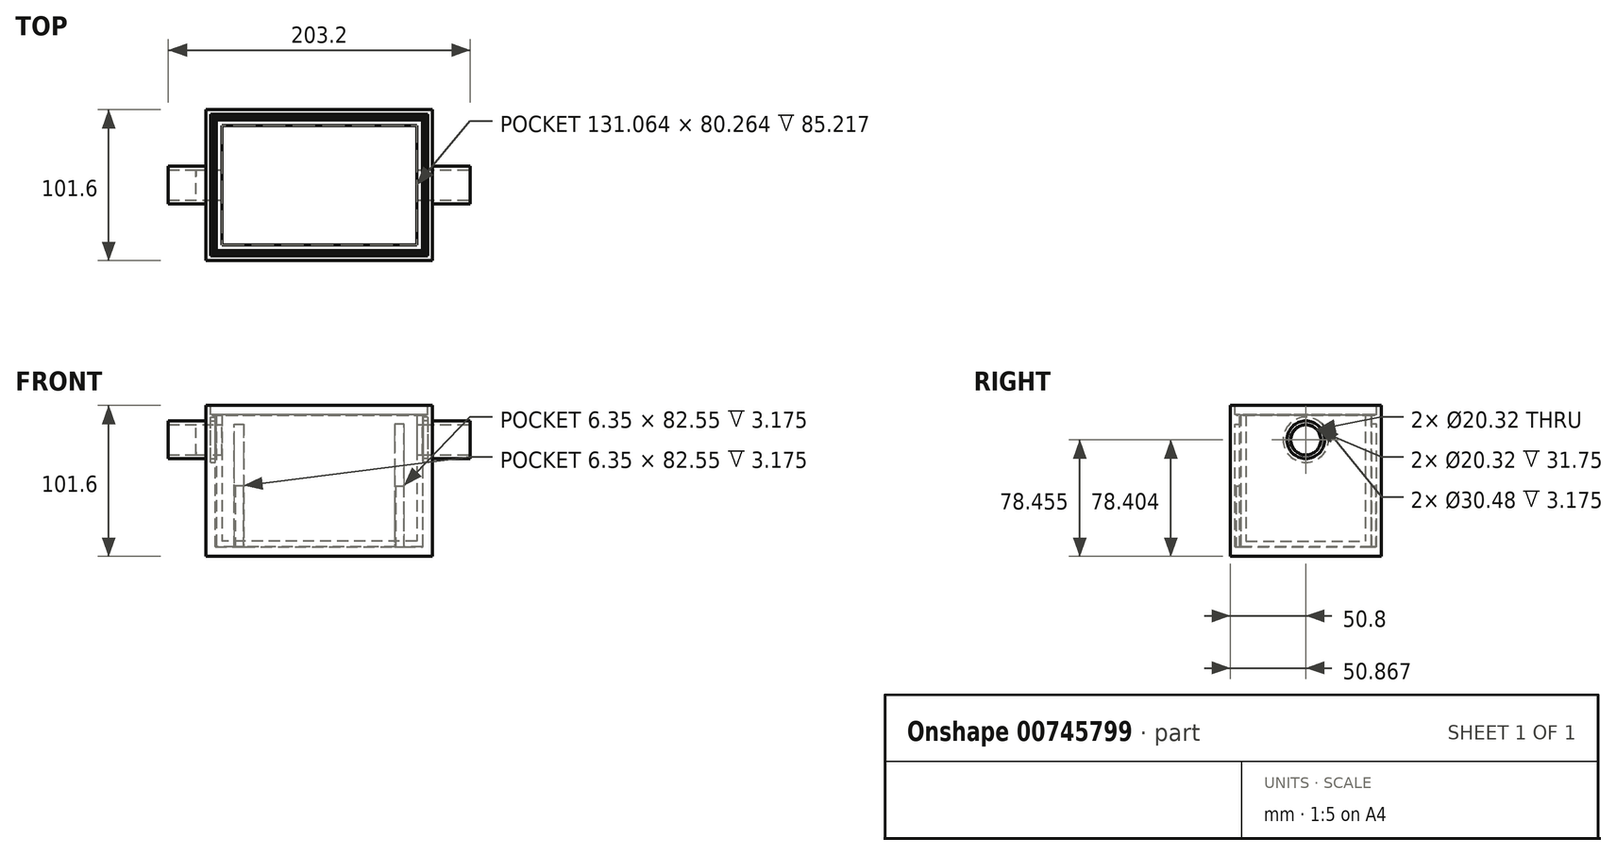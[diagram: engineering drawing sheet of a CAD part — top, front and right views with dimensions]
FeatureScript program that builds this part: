
annotation { "Feature Type Name" : "Feature", "Feature Type Description" : "" }
export const myFeature = defineFeature(function(context is Context, id is Id, definition is map)
    precondition{}
    {
        {
            var Q0;
            Q0=qCreatedBy(makeId("Front.planeOp"),FACE);
            var sketch = newSketch(context, id + "F0", { "sketchPlane" : qUnion([Q0])});
            skLineSegment(sketch, "E0.bottom", {"start": v(-76.2, 50.8) * mm, "end": v(76.2, 50.8) * mm});
            skLineSegment(sketch, "E0.top", {"start": v(-76.2, -50.8) * mm, "end": v(76.2, -50.8) * mm});
            skLineSegment(sketch, "E0.left", {"start": v(-76.2, 50.8) * mm, "end": v(-76.2, -50.8) * mm});
            skLineSegment(sketch, "E0.right", {"start": v(76.2, 50.8) * mm, "end": v(76.2, -50.8) * mm});
            skPoint(sketch, "E0.middle", {"position": v(0, 0) * mm});
            skSolve(sketch);
        }
        {
            var Q0;
            Q0 = qSketchRegion(id + "F0", true);
            extrude(context, id + "F1", {"entities" : qUnion([Q0]), "depth" : 101.6 * mm, "offsetDistance" : 25.4 * mm});
        }
        {
            var Q0;
            Q0=makeQuery(id+"F1.opExtrude","SWEPT_FACE",FACE,{"disambiguationData":[OSD([sQuery(id+"F0.wireOp",EDGE,"E0.left")])]});
            var sketch = newSketch(context, id + "F2", { "sketchPlane" : qUnion([Q0])});
            skCircle(sketch, "E1", {"center": v(50.8, 27.65) * mm, "radius": 12.7 * mm});
            skPoint(sketch, "E1.centerSnap0", {"position": v(50.8, 50.8) * mm});
            skCircle(sketch, "E2", {"center": v(50.8, 27.65) * mm, "radius": 10.16 * mm});
            skSolve(sketch);
        }
        {
            var Q0;
            Q0 = qSketchRegion(id + "F2", true);
            extrude(context, id + "F3", {"entities" : qUnion([Q0]), "operationType" : NewBodyOperationType.ADD, "depth" : 25.4 * mm, "offsetDistance" : 25.4 * mm, "hasSecondDirection" : true, "secondDirectionOppositeDirection" : true, "secondDirectionDepth" : 177.8 * mm});
        }
        {
            var Q0;
            Q0=makeQuery(id+"F3.boolean.opBoolean","SPLIT",FACE,{"disambiguationData":[TD([makeQuery(id+"F3.opExtrude","SWEPT_FACE",FACE,{"disambiguationData":[OSD([sQuery(id+"F2.wireOp",EDGE,"E2")])]})])],"derivedFrom":makeQuery(id+"F1.opExtrude","SWEPT_FACE",FACE,{"disambiguationData":[OSD([sQuery(id+"F0.wireOp",EDGE,"E0.left")])]})});
            var sketch = newSketch(context, id + "F4", { "sketchPlane" : qUnion([Q0])});
            skCircle(sketch, "E3", {"center": v(50.8, 27.65) * mm, "radius": 10.16 * mm});
            skPoint(sketch, "E3.first.point", {"position": v(44.09, 35.28) * mm});
            skPoint(sketch, "E3.second.point", {"position": v(54.89, 36.96) * mm});
            skPoint(sketch, "E3.third.point", {"position": v(59.33, 33.17) * mm});
            skSolve(sketch);
        }
        {
            var Q0;
            Q0 = qSketchRegion(id + "F4", true);
            extrude(context, id + "F5", {"entities" : qUnion([Q0]), "operationType" : NewBodyOperationType.REMOVE, "oppositeDirection" : true, "depth" : 152.4 * mm, "offsetDistance" : 25.4 * mm});
        }
        {
            var Q0;
            Q0=makeQuery(id+"F1.opExtrude","SWEPT_FACE",FACE,{"disambiguationData":[OSD([sQuery(id+"F0.wireOp",EDGE,"E0.bottom")])]});
            var sketch = newSketch(context, id + "F6", { "sketchPlane" : qUnion([Q0])});
            skLineSegment(sketch, "E4.bottom", {"start": v(-69.85, -6.35) * mm, "end": v(69.85, -6.35) * mm});
            skLineSegment(sketch, "E4.top", {"start": v(-69.85, -95.25) * mm, "end": v(69.85, -95.25) * mm});
            skLineSegment(sketch, "E4.left", {"start": v(-69.85, -6.35) * mm, "end": v(-69.85, -95.25) * mm});
            skLineSegment(sketch, "E4.right", {"start": v(69.85, -6.35) * mm, "end": v(69.85, -95.25) * mm});
            skPoint(sketch, "E4.middle", {"position": v(0, -50.8) * mm});
            skPoint(sketch, "E4.middle.positionSnap0", {"position": v(-76.2, -50.8) * mm});
            skPoint(sketch, "E4.middle.positionSnap1", {"position": v(0, 0) * mm});
            skPoint(sketch, "E4.centerSnap0", {"position": v(-76.2, -50.8) * mm});
            skPoint(sketch, "E4.centerSnap1", {"position": v(0, 0) * mm});
            skSolve(sketch);
        }
        {
            var Q0;
            Q0 = qSketchRegion(id + "F6", true);
            extrude(context, id + "F7", {"entities" : qUnion([Q0]), "operationType" : NewBodyOperationType.REMOVE, "oppositeDirection" : true, "depth" : 95.25 * mm, "offsetDistance" : 25.4 * mm});
        }
        {
            var Q0;
            Q0=makeQuery(id+"F1.opExtrude","SWEPT_FACE",FACE,{"disambiguationData":[OSD([sQuery(id+"F0.wireOp",EDGE,"E0.bottom")])]});
            var sketch = newSketch(context, id + "F8", { "sketchPlane" : qUnion([Q0])});
            skLineSegment(sketch, "E5.bottom", {"start": v(73.03, -3.18) * mm, "end": v(-73.03, -3.18) * mm});
            skLineSegment(sketch, "E5.top", {"start": v(73.03, -98.43) * mm, "end": v(-73.03, -98.43) * mm});
            skLineSegment(sketch, "E5.left", {"start": v(73.03, -3.18) * mm, "end": v(73.03, -98.43) * mm});
            skLineSegment(sketch, "E5.right", {"start": v(-73.03, -3.18) * mm, "end": v(-73.03, -98.43) * mm});
            skPoint(sketch, "E5.middle", {"position": v(0, -50.8) * mm});
            skPoint(sketch, "E5.middle.positionSnap0", {"position": v(-69.85, -50.8) * mm});
            skPoint(sketch, "E5.centerSnap0", {"position": v(-69.85, -50.8) * mm});
            skSolve(sketch);
        }
        {
            var Q0;
            Q0 = qSketchRegion(id + "F8", true);
            extrude(context, id + "F9", {"entities" : qUnion([Q0]), "operationType" : NewBodyOperationType.REMOVE, "oppositeDirection" : true, "depth" : 6.35 * mm, "offsetDistance" : 25.4 * mm});
        }
        {
            var Q0;
            Q0=makeQuery(id+"F7.boolean.opBoolean","COPY",FACE,{"derivedFrom":makeQuery(id+"F7.opExtrude","SWEPT_FACE",FACE,{"disambiguationData":[OSD([sQuery(id+"F6.wireOp",EDGE,"E4.bottom")])]})});
            var sketch = newSketch(context, id + "F10", { "sketchPlane" : qUnion([Q0])});
            skLineSegment(sketch, "E6", {"start": v(-57.15, -44.45) * mm, "end": v(-57.15, 38.1) * mm});
            skLineSegment(sketch, "E7", {"start": v(-57.15, 38.1) * mm, "end": v(-50.8, 38.1) * mm});
            skLineSegment(sketch, "E8", {"start": v(-50.8, 38.1) * mm, "end": v(-50.8, -44.45) * mm});
            skLineSegment(sketch, "E9", {"start": v(-50.8, -44.45) * mm, "end": v(-57.15, -44.45) * mm});
            skLineSegment(sketch, "E10", {"start": v(57.15, -44.45) * mm, "end": v(57.15, 38.1) * mm});
            skLineSegment(sketch, "E11", {"start": v(57.15, 38.1) * mm, "end": v(50.8, 38.1) * mm});
            skLineSegment(sketch, "E12", {"start": v(50.8, 38.1) * mm, "end": v(50.8, -44.45) * mm});
            skLineSegment(sketch, "E13", {"start": v(50.8, -44.45) * mm, "end": v(57.15, -44.45) * mm});
            skSolve(sketch);
        }
        {
            var Q0;
            Q0 = qSketchRegion(id + "F10", true);
            extrude(context, id + "F11", {"entities" : qUnion([Q0]), "operationType" : NewBodyOperationType.REMOVE, "oppositeDirection" : true, "depth" : 3.17 * mm, "offsetDistance" : 25.4 * mm});
        }
        {
            var Q0;
            Q0=makeQuery(id+"F9.boolean.opBoolean","COPY",FACE,{"derivedFrom":makeQuery(id+"F9.opExtrude","CAP_FACE",FACE,{"disambiguationData":[OSD([sQuery(id+"F8.wireOp",EDGE,"E5.bottom"),sQuery(id+"F8.wireOp",EDGE,"E5.top"),sQuery(id+"F8.wireOp",EDGE,"E5.left"),sQuery(id+"F8.wireOp",EDGE,"E5.right")])],"isStart":false})});
            var sketch = newSketch(context, id + "F12", { "sketchPlane" : qUnion([Q0])});
            skLineSegment(sketch, "E14.bottom", {"start": v(71.75, -4.45) * mm, "end": v(-71.76, -4.45) * mm});
            skLineSegment(sketch, "E14.top", {"start": v(71.75, -97.16) * mm, "end": v(-71.76, -97.16) * mm});
            skLineSegment(sketch, "E14.left", {"start": v(71.75, -4.45) * mm, "end": v(71.75, -97.16) * mm});
            skLineSegment(sketch, "E14.right", {"start": v(-71.76, -4.45) * mm, "end": v(-71.76, -97.16) * mm});
            skPoint(sketch, "E14.middle", {"position": v(0, -50.8) * mm});
            skPoint(sketch, "E14.middle.positionSnap0", {"position": v(-69.85, -50.8) * mm});
            skPoint(sketch, "E14.middle.positionSnap1", {"position": v(0, -95.25) * mm});
            skPoint(sketch, "E14.centerSnap0", {"position": v(-69.85, -50.8) * mm});
            skPoint(sketch, "E14.centerSnap1", {"position": v(0, -95.25) * mm});
            skLineSegment(sketch, "E15.bottom", {"start": v(71.12, -5.08) * mm, "end": v(-71.12, -5.08) * mm});
            skLineSegment(sketch, "E15.top", {"start": v(71.12, -96.52) * mm, "end": v(-71.12, -96.52) * mm});
            skLineSegment(sketch, "E15.left", {"start": v(71.12, -5.08) * mm, "end": v(71.12, -96.52) * mm});
            skLineSegment(sketch, "E15.right", {"start": v(-71.12, -5.08) * mm, "end": v(-71.12, -96.52) * mm});
            skSolve(sketch);
        }
        {
            var Q0;
            Q0 = qSketchRegion(id + "F12", true);
            extrude(context, id + "F13", {"entities" : qUnion([Q0]), "operationType" : NewBodyOperationType.REMOVE, "oppositeDirection" : true, "depth" : 0.64 * mm, "offsetDistance" : 25.4 * mm});
        }
        {
            var Q0;
            Q0=makeQuery(id+"F7.boolean.opBoolean","COPY",FACE,{"derivedFrom":makeQuery(id+"F7.opExtrude","SWEPT_FACE",FACE,{"disambiguationData":[OSD([sQuery(id+"F6.wireOp",EDGE,"E4.left")])]})});
            var sketch = newSketch(context, id + "F14", { "sketchPlane" : qUnion([Q0])});
            skPoint(sketch, "E16", {"position": v(-41.68, 36.5) * mm});
            skPoint(sketch, "E17", {"position": v(-63.23, 30.24) * mm});
            skPoint(sketch, "E18", {"position": v(-45.27, 16.22) * mm});
            skCircle(sketch, "E19", {"center": v(-50.8, 27.65) * mm, "radius": 12.7 * mm});
            skPoint(sketch, "E20", {"position": v(-39.81, 38.22) * mm});
            skPoint(sketch, "E21", {"position": v(-43.83, 14.1) * mm});
            skPoint(sketch, "E22", {"position": v(-65.64, 31.11) * mm});
            skCircle(sketch, "E23", {"center": v(-50.8, 27.65) * mm, "radius": 15.24 * mm});
            skSolve(sketch);
        }
        {
            var Q0;
            Q0 = qSketchRegion(id + "F14", true);
            extrude(context, id + "F15", {"entities" : qUnion([Q0]), "operationType" : NewBodyOperationType.REMOVE, "oppositeDirection" : true, "depth" : 3.17 * mm, "offsetDistance" : 25.4 * mm});
        }
        {
            var Q0;
            Q0=makeQuery(id+"F7.boolean.opBoolean","COPY",FACE,{"derivedFrom":makeQuery(id+"F7.opExtrude","SWEPT_FACE",FACE,{"disambiguationData":[OSD([sQuery(id+"F6.wireOp",EDGE,"E4.right")])]})});
            var sketch = newSketch(context, id + "F16", { "sketchPlane" : qUnion([Q0])});
            skPoint(sketch, "E24", {"position": v(38.15, 28.8) * mm});
            skPoint(sketch, "E25", {"position": v(35.6, 28.66) * mm});
            skPoint(sketch, "E26", {"position": v(54.32, 15.45) * mm});
            skPoint(sketch, "E27", {"position": v(54.56, 12.88) * mm});
            skPoint(sketch, "E28", {"position": v(58.17, 38) * mm});
            skPoint(sketch, "E29", {"position": v(59.43, 40.22) * mm});
            skCircle(sketch, "E30", {"center": v(50.8, 27.65) * mm, "radius": 12.7 * mm});
            skCircle(sketch, "E31", {"center": v(50.8, 27.65) * mm, "radius": 15.24 * mm});
            skSolve(sketch);
        }
        {
            var Q0;
            Q0 = qSketchRegion(id + "F16", true);
            extrude(context, id + "F17", {"entities" : qUnion([Q0]), "operationType" : NewBodyOperationType.REMOVE, "oppositeDirection" : true, "depth" : 3.17 * mm, "offsetDistance" : 25.4 * mm});
        }
        {
            var Q0;
            Q0=makeQuery(id+"F7.boolean.opBoolean","COPY",FACE,{"derivedFrom":makeQuery(id+"F7.opExtrude","SWEPT_FACE",FACE,{"disambiguationData":[OSD([sQuery(id+"F6.wireOp",EDGE,"E4.top")])]})});
            var sketch = newSketch(context, id + "F18", { "sketchPlane" : qUnion([Q0])});
            skLineSegment(sketch, "E32", {"start": v(57.15, -44.45) * mm, "end": v(57.15, 38.1) * mm});
            skLineSegment(sketch, "E33", {"start": v(57.15, 38.1) * mm, "end": v(50.8, 38.1) * mm});
            skLineSegment(sketch, "E34", {"start": v(50.8, 38.1) * mm, "end": v(50.8, -44.45) * mm});
            skLineSegment(sketch, "E35", {"start": v(-57.15, -44.45) * mm, "end": v(-57.15, 38.1) * mm});
            skLineSegment(sketch, "E36", {"start": v(-57.15, 38.1) * mm, "end": v(-50.8, 38.1) * mm});
            skLineSegment(sketch, "E37", {"start": v(-50.8, 38.1) * mm, "end": v(-50.8, -44.45) * mm});
            skLineSegment(sketch, "E38", {"start": v(57.15, -44.45) * mm, "end": v(50.8, -44.45) * mm});
            skLineSegment(sketch, "E39", {"start": v(-57.15, -44.45) * mm, "end": v(-50.8, -44.45) * mm});
            skSolve(sketch);
        }
        {
            var Q0;
            Q0 = qSketchRegion(id + "F18", true);
            extrude(context, id + "F19", {"entities" : qUnion([Q0]), "operationType" : NewBodyOperationType.REMOVE, "oppositeDirection" : true, "depth" : 3.17 * mm, "offsetDistance" : 25.4 * mm});
        }
        {
            var Q0;
            Q0=makeQuery(id+"F19.boolean.opBoolean","MERGE",FACE,{"derivedFrom":[makeQuery(id+"F11.boolean.opBoolean","MERGE",FACE,{"derivedFrom":[makeQuery(id+"F7.boolean.opBoolean","COPY",FACE,{"derivedFrom":makeQuery(id+"F7.opExtrude","CAP_FACE",FACE,{"disambiguationData":[OSD([sQuery(id+"F6.wireOp",EDGE,"E4.bottom"),sQuery(id+"F6.wireOp",EDGE,"E4.top"),sQuery(id+"F6.wireOp",EDGE,"E4.left"),sQuery(id+"F6.wireOp",EDGE,"E4.right")])],"isStart":false})}),makeQuery(id+"F11.opExtrude","SWEPT_FACE",FACE,{"disambiguationData":[OSD([sQuery(id+"F10.wireOp",EDGE,"E9")])]}),makeQuery(id+"F11.opExtrude","SWEPT_FACE",FACE,{"disambiguationData":[OSD([sQuery(id+"F10.wireOp",EDGE,"E13")])]})]}),makeQuery(id+"F19.opExtrude","SWEPT_FACE",FACE,{"disambiguationData":[OSD([sQuery(id+"F18.wireOp",EDGE,"E38")])]}),makeQuery(id+"F19.opExtrude","SWEPT_FACE",FACE,{"disambiguationData":[OSD([sQuery(id+"F18.wireOp",EDGE,"E39")])]})]});
            var sketch = newSketch(context, id + "F20", { "sketchPlane" : qUnion([Q0])});
            skLineSegment(sketch, "E40", {"start": v(56.64, -97.92) * mm, "end": v(56.64, -94.74) * mm});
            skLineSegment(sketch, "E41", {"start": v(56.64, -94.74) * mm, "end": v(69.34, -94.74) * mm});
            skLineSegment(sketch, "E42", {"start": v(69.34, -94.74) * mm, "end": v(69.34, -6.86) * mm});
            skLineSegment(sketch, "E43", {"start": v(69.34, -6.86) * mm, "end": v(56.64, -6.86) * mm});
            skLineSegment(sketch, "E44", {"start": v(56.64, -6.86) * mm, "end": v(56.64, -3.68) * mm});
            skLineSegment(sketch, "E45", {"start": v(56.64, -3.68) * mm, "end": v(51.3, -3.68) * mm});
            skLineSegment(sketch, "E46", {"start": v(51.3, -3.68) * mm, "end": v(51.3, -6.86) * mm});
            skLineSegment(sketch, "E47", {"start": v(51.3, -6.86) * mm, "end": v(-51.3, -6.86) * mm});
            skLineSegment(sketch, "E48", {"start": v(-51.3, -6.86) * mm, "end": v(-51.3, -3.68) * mm});
            skLineSegment(sketch, "E49", {"start": v(-51.3, -3.68) * mm, "end": v(-56.64, -3.68) * mm});
            skLineSegment(sketch, "E50", {"start": v(-56.64, -3.68) * mm, "end": v(-56.64, -6.86) * mm});
            skLineSegment(sketch, "E51", {"start": v(-56.64, -6.86) * mm, "end": v(-69.34, -6.86) * mm});
            skLineSegment(sketch, "E52", {"start": v(-69.34, -6.86) * mm, "end": v(-69.34, -94.74) * mm});
            skLineSegment(sketch, "E53", {"start": v(-69.34, -94.74) * mm, "end": v(-56.64, -94.74) * mm});
            skLineSegment(sketch, "E54", {"start": v(-56.64, -94.74) * mm, "end": v(-56.64, -97.92) * mm});
            skLineSegment(sketch, "E55", {"start": v(-56.64, -97.92) * mm, "end": v(-51.3, -97.92) * mm});
            skLineSegment(sketch, "E56", {"start": v(-51.3, -97.92) * mm, "end": v(-51.3, -94.74) * mm});
            skLineSegment(sketch, "E57", {"start": v(-51.3, -94.74) * mm, "end": v(51.3, -94.74) * mm});
            skLineSegment(sketch, "E58", {"start": v(51.3, -94.74) * mm, "end": v(51.3, -97.92) * mm});
            skLineSegment(sketch, "E59", {"start": v(51.3, -97.92) * mm, "end": v(56.64, -97.92) * mm});
            skSolve(sketch);
        }
        {
            var Q0;
            Q0 = qSketchRegion(id + "F20", true);
            extrude(context, id + "F21", {"entities" : qUnion([Q0]), "depth" : 82.04 * mm, "offsetDistance" : 25.4 * mm});
        }
        {
            var Q0;
            Q0=makeQuery(id+"F21.opExtrude","CAP_FACE",FACE,{"disambiguationData":[OSD([sQuery(id+"F20.wireOp",EDGE,"E40"),sQuery(id+"F20.wireOp",EDGE,"E41"),sQuery(id+"F20.wireOp",EDGE,"E42"),sQuery(id+"F20.wireOp",EDGE,"E43"),sQuery(id+"F20.wireOp",EDGE,"E44"),sQuery(id+"F20.wireOp",EDGE,"E45"),sQuery(id+"F20.wireOp",EDGE,"E46"),sQuery(id+"F20.wireOp",EDGE,"E47"),sQuery(id+"F20.wireOp",EDGE,"E48"),sQuery(id+"F20.wireOp",EDGE,"E49"),sQuery(id+"F20.wireOp",EDGE,"E50"),sQuery(id+"F20.wireOp",EDGE,"E51"),sQuery(id+"F20.wireOp",EDGE,"E52"),sQuery(id+"F20.wireOp",EDGE,"E53"),sQuery(id+"F20.wireOp",EDGE,"E54"),sQuery(id+"F20.wireOp",EDGE,"E55"),sQuery(id+"F20.wireOp",EDGE,"E56"),sQuery(id+"F20.wireOp",EDGE,"E57"),sQuery(id+"F20.wireOp",EDGE,"E58"),sQuery(id+"F20.wireOp",EDGE,"E59")])],"isStart":false});
            var sketch = newSketch(context, id + "F22", { "sketchPlane" : qUnion([Q0])});
            skLineSegment(sketch, "E60.bottom", {"start": v(51.3, -6.86) * mm, "end": v(56.64, -6.86) * mm});
            skLineSegment(sketch, "E60.top", {"start": v(51.3, -3.68) * mm, "end": v(56.64, -3.68) * mm});
            skLineSegment(sketch, "E60.left", {"start": v(51.3, -6.86) * mm, "end": v(51.3, -3.68) * mm});
            skLineSegment(sketch, "E60.right", {"start": v(56.64, -6.86) * mm, "end": v(56.64, -3.68) * mm});
            skLineSegment(sketch, "E61.bottom", {"start": v(56.64, -94.74) * mm, "end": v(51.3, -94.74) * mm});
            skLineSegment(sketch, "E61.top", {"start": v(56.64, -97.92) * mm, "end": v(51.3, -97.92) * mm});
            skLineSegment(sketch, "E61.left", {"start": v(56.64, -94.74) * mm, "end": v(56.64, -97.92) * mm});
            skLineSegment(sketch, "E61.right", {"start": v(51.3, -94.74) * mm, "end": v(51.3, -97.92) * mm});
            skLineSegment(sketch, "E62.bottom", {"start": v(-51.3, -94.74) * mm, "end": v(-56.64, -94.74) * mm});
            skLineSegment(sketch, "E62.top", {"start": v(-51.3, -97.92) * mm, "end": v(-56.64, -97.92) * mm});
            skLineSegment(sketch, "E62.left", {"start": v(-51.3, -94.74) * mm, "end": v(-51.3, -97.92) * mm});
            skLineSegment(sketch, "E62.right", {"start": v(-56.64, -94.74) * mm, "end": v(-56.64, -97.92) * mm});
            skLineSegment(sketch, "E63.bottom", {"start": v(-56.64, -6.86) * mm, "end": v(-51.3, -6.86) * mm});
            skLineSegment(sketch, "E63.top", {"start": v(-56.64, -3.68) * mm, "end": v(-51.3, -3.68) * mm});
            skLineSegment(sketch, "E63.left", {"start": v(-56.64, -6.86) * mm, "end": v(-56.64, -3.68) * mm});
            skLineSegment(sketch, "E63.right", {"start": v(-51.3, -6.86) * mm, "end": v(-51.3, -3.68) * mm});
            skSolve(sketch);
        }
        {
            var Q0;
            Q0 = qSketchRegion(id + "F22", true);
            extrude(context, id + "F23", {"entities" : qUnion([Q0]), "operationType" : NewBodyOperationType.REMOVE, "oppositeDirection" : true, "depth" : 41.02 * mm, "offsetDistance" : 25.4 * mm});
        }
        {
            var Q0;
            Q0=makeQuery(id+"F21.opExtrude","CAP_FACE",FACE,{"disambiguationData":[OSD([sQuery(id+"F20.wireOp",EDGE,"E40"),sQuery(id+"F20.wireOp",EDGE,"E41"),sQuery(id+"F20.wireOp",EDGE,"E42"),sQuery(id+"F20.wireOp",EDGE,"E43"),sQuery(id+"F20.wireOp",EDGE,"E44"),sQuery(id+"F20.wireOp",EDGE,"E45"),sQuery(id+"F20.wireOp",EDGE,"E46"),sQuery(id+"F20.wireOp",EDGE,"E47"),sQuery(id+"F20.wireOp",EDGE,"E48"),sQuery(id+"F20.wireOp",EDGE,"E49"),sQuery(id+"F20.wireOp",EDGE,"E50"),sQuery(id+"F20.wireOp",EDGE,"E51"),sQuery(id+"F20.wireOp",EDGE,"E52"),sQuery(id+"F20.wireOp",EDGE,"E53"),sQuery(id+"F20.wireOp",EDGE,"E54"),sQuery(id+"F20.wireOp",EDGE,"E55"),sQuery(id+"F20.wireOp",EDGE,"E56"),sQuery(id+"F20.wireOp",EDGE,"E57"),sQuery(id+"F20.wireOp",EDGE,"E58"),sQuery(id+"F20.wireOp",EDGE,"E59")])],"isStart":false});
            shell(context, id + "F24", {"entities" : qUnion([Q0]), "thickness" : 3.8 * mm});
        }
        {
            var Q0;
            Q0=makeQuery(id+"F21.opExtrude","CAP_FACE",FACE,{"disambiguationData":[OSD([sQuery(id+"F20.wireOp",EDGE,"E40"),sQuery(id+"F20.wireOp",EDGE,"E41"),sQuery(id+"F20.wireOp",EDGE,"E42"),sQuery(id+"F20.wireOp",EDGE,"E43"),sQuery(id+"F20.wireOp",EDGE,"E44"),sQuery(id+"F20.wireOp",EDGE,"E45"),sQuery(id+"F20.wireOp",EDGE,"E46"),sQuery(id+"F20.wireOp",EDGE,"E47"),sQuery(id+"F20.wireOp",EDGE,"E48"),sQuery(id+"F20.wireOp",EDGE,"E49"),sQuery(id+"F20.wireOp",EDGE,"E50"),sQuery(id+"F20.wireOp",EDGE,"E51"),sQuery(id+"F20.wireOp",EDGE,"E52"),sQuery(id+"F20.wireOp",EDGE,"E53"),sQuery(id+"F20.wireOp",EDGE,"E54"),sQuery(id+"F20.wireOp",EDGE,"E55"),sQuery(id+"F20.wireOp",EDGE,"E56"),sQuery(id+"F20.wireOp",EDGE,"E57"),sQuery(id+"F20.wireOp",EDGE,"E58"),sQuery(id+"F20.wireOp",EDGE,"E59")])],"isStart":false});
            var sketch = newSketch(context, id + "F25", { "sketchPlane" : qUnion([Q0])});
            skLineSegment(sketch, "E64.bottom", {"start": v(-65.53, -10.67) * mm, "end": v(65.53, -10.67) * mm});
            skLineSegment(sketch, "E64.top", {"start": v(-65.53, -90.93) * mm, "end": v(65.53, -90.93) * mm});
            skLineSegment(sketch, "E64.left", {"start": v(-65.53, -10.67) * mm, "end": v(-65.53, -90.93) * mm});
            skLineSegment(sketch, "E64.right", {"start": v(65.53, -10.67) * mm, "end": v(65.53, -90.93) * mm});
            skLineSegment(sketch, "E65.bottom", {"start": v(69.34, -94.74) * mm, "end": v(-69.34, -94.74) * mm});
            skLineSegment(sketch, "E65.top", {"start": v(69.34, -6.86) * mm, "end": v(-69.34, -6.86) * mm});
            skLineSegment(sketch, "E65.left", {"start": v(69.34, -94.74) * mm, "end": v(69.34, -6.86) * mm});
            skLineSegment(sketch, "E65.right", {"start": v(-69.34, -94.74) * mm, "end": v(-69.34, -6.86) * mm});
            skSolve(sketch);
        }
        {
            var Q0;
            Q0 = qSketchRegion(id + "F25", true);
            extrude(context, id + "F26", {"entities" : qUnion([Q0]), "operationType" : NewBodyOperationType.ADD, "depth" : 7 * mm, "offsetDistance" : 25.4 * mm});
        }
        {
            var Q0;
            Q0=makeQuery(id+"F26.boolean.opBoolean","MERGE",FACE,{"derivedFrom":[makeQuery(id+"F21.opExtrude","SWEPT_FACE",FACE,{"disambiguationData":[OSD([sQuery(id+"F20.wireOp",EDGE,"E42")])]}),makeQuery(id+"F26.opExtrude","SWEPT_FACE",FACE,{"disambiguationData":[OSD([sQuery(id+"F25.wireOp",EDGE,"E65.left")])]})]});
            var sketch = newSketch(context, id + "F27", { "sketchPlane" : qUnion([Q0])});
            skCircle(sketch, "E66", {"center": v(-50.73, 27.6) * mm, "radius": 10.16 * mm});
            skPoint(sketch, "E66.first.point", {"position": v(-56.97, 35.63) * mm});
            skPoint(sketch, "E66.second.point", {"position": v(-54.58, 18.2) * mm});
            skPoint(sketch, "E66.third.point", {"position": v(-40.58, 27.94) * mm});
            skSolve(sketch);
        }
        {
            var Q0;
            Q0 = qSketchRegion(id + "F27", true);
            extrude(context, id + "F28", {"entities" : qUnion([Q0]), "operationType" : NewBodyOperationType.REMOVE, "oppositeDirection" : true, "depth" : 152.4 * mm, "offsetDistance" : 25.4 * mm});
        }
    });
